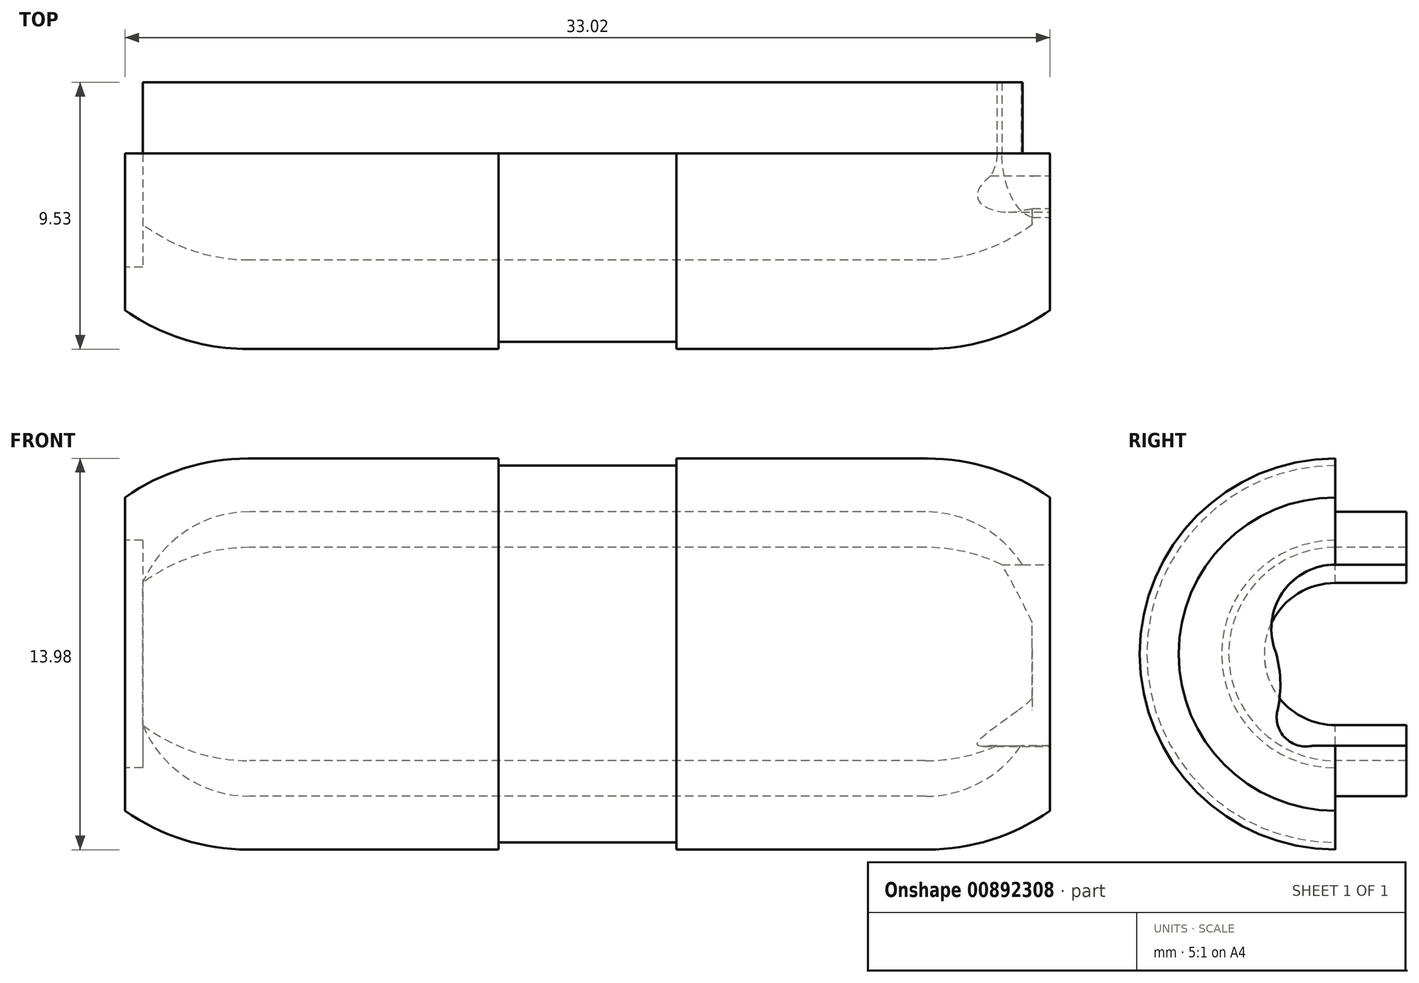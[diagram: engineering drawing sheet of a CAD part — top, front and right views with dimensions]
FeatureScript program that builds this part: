
annotation { "Feature Type Name" : "Feature", "Feature Type Description" : "" }
export const myFeature = defineFeature(function(context is Context, id is Id, definition is map)
    precondition{}
    {
        {
            var Q0;
            Q0=qCreatedBy(makeId("Front.planeOp"),FACE);
            var sketch = newSketch(context, id + "F0", { "sketchPlane" : qUnion([Q0])});
            skLineSegment(sketch, "E0.top", {"start": v(12.12, 6.98) * mm, "end": v(-12.12, 6.98) * mm});
            skPoint(sketch, "E0.middle", {"position": v(0, 0) * mm});
            skArc(sketch, "E1.filletArc", {"start": v(-12.12, 6.98) * mm, "mid": v(-16.24, 5.78) * mm, "end": v(-19.05, 2.54) * mm});
            skArc(sketch, "E2.filletArc", {"start": v(19.05, 2.54) * mm, "mid": v(16.24, 5.78) * mm, "end": v(12.12, 6.98) * mm});
            skLineSegment(sketch, "E3.top", {"start": v(12.06, 3.8) * mm, "end": v(-12.06, 3.8) * mm});
            skArc(sketch, "E4.filletArc", {"start": v(-12.06, 3.8) * mm, "mid": v(-14.07, 3.48) * mm, "end": v(-15.88, 2.54) * mm});
            skArc(sketch, "E5.filletArc", {"start": v(15.88, 2.54) * mm, "mid": v(14.07, 3.48) * mm, "end": v(12.06, 3.8) * mm});
            skLineSegment(sketch, "E6.top", {"start": v(-19.05, 2.54) * mm, "end": v(-15.88, 2.54) * mm});
            skPoint(sketch, "E7.orphan", {"position": v(-47.42, 2.54) * mm});
            skLineSegment(sketch, "E8.trimOffspring", {"start": v(15.88, 2.54) * mm, "end": v(19.05, 2.54) * mm});
            skSolve(sketch);
        }
        {
            var Q0;
            Q0=qCreatedBy(makeId("Top.planeOp"),FACE);
            var sketch = newSketch(context, id + "F1", { "sketchPlane" : qUnion([Q0])});
            skLineSegment(sketch, "E9", {"start": v(-41.86, 0) * mm, "end": v(38.58, 0) * mm, "construction": true});
            skSolve(sketch);
        }
        {
            var Q0;
            Q0 = qSketchRegion(id + "F0", true);
            var Q1;
            Q1=sQuery(id+"F1.wireOp",EDGE,"E9");
            revolve(context, id + "F2", {"surfaceOperationType" : NewSurfaceOperationType.NEW, "entities" : qUnion([Q0]), "axis" : qUnion([Q1]), "revolveType" : RevolveType.ONE_DIRECTION, "angle" : 180 * degree});
        }
        {
            var Q0;
            Q0=makeQuery(id+"F2.opRevolve","CAP_FACE",FACE,{"disambiguationData":[OSD([sQuery(id+"F0.wireOp",EDGE,"E0.top"),sQuery(id+"F0.wireOp",EDGE,"E1.filletArc"),sQuery(id+"F0.wireOp",EDGE,"E2.filletArc"),sQuery(id+"F0.wireOp",EDGE,"E3.top"),sQuery(id+"F0.wireOp",EDGE,"E4.filletArc"),sQuery(id+"F0.wireOp",EDGE,"E5.filletArc"),sQuery(id+"F0.wireOp",EDGE,"JIvlJlBu-vfLA-I6Gr-C8jU-59FBPmd7U8bv"),sQuery(id+"F0.wireOp",EDGE,"RInppC3X-QeJU-EZpC-KpJT-0cWvms3T49e7")])],"isStart":true});
            var sketch = newSketch(context, id + "F3", { "sketchPlane" : qUnion([Q0])});
            skLineSegment(sketch, "E10", {"start": v(-12.06, -3.8) * mm, "end": v(12.06, -3.8) * mm});
            skPoint(sketch, "E11.visualSharp", {"position": v(-15.87, -14.87) * mm});
            skArc(sketch, "E11.filletArc", {"start": v(-15.88, -2.54) * mm, "mid": v(-14.07, -3.48) * mm, "end": v(-12.06, -3.8) * mm});
            skArc(sketch, "E12", {"start": v(12.06, -3.8) * mm, "mid": v(14.07, -3.48) * mm, "end": v(15.87, -2.54) * mm});
            skLineSegment(sketch, "E13", {"start": v(-12.06, -5.08) * mm, "end": v(12.06, -5.08) * mm});
            skPoint(sketch, "E14.visualSharp", {"position": v(-15.87, -15.92) * mm});
            skArc(sketch, "E14.filletArc", {"start": v(-15.88, -2.54) * mm, "mid": v(-14.35, -4.39) * mm, "end": v(-12.06, -5.08) * mm});
            skPoint(sketch, "E15.visualSharp", {"position": v(22.86, -13.97) * mm});
            skArc(sketch, "E15.filletArc", {"start": v(12.06, -5.08) * mm, "mid": v(14.35, -4.39) * mm, "end": v(15.87, -2.54) * mm});
            skArc(sketch, "E16.MirrorCS", {"start": v(12.06, 5.08) * mm, "mid": v(14.35, 4.39) * mm, "end": v(15.87, 2.54) * mm});
            skArc(sketch, "E17.MirrorCS", {"start": v(12.06, 3.8) * mm, "mid": v(14.07, 3.48) * mm, "end": v(15.87, 2.54) * mm});
            skArc(sketch, "E18.MirrorCS", {"start": v(-15.88, 2.54) * mm, "mid": v(-14.35, 4.39) * mm, "end": v(-12.06, 5.08) * mm});
            skArc(sketch, "E19.MirrorCS", {"start": v(-15.88, 2.54) * mm, "mid": v(-14.07, 3.48) * mm, "end": v(-12.06, 3.8) * mm});
            skLineSegment(sketch, "E20.MirrorCS", {"start": v(-12.06, 5.08) * mm, "end": v(12.06, 5.08) * mm});
            skLineSegment(sketch, "E21.MirrorCS", {"start": v(-12.06, 3.8) * mm, "end": v(12.06, 3.8) * mm});
            skSolve(sketch);
        }
        {
            var Q0;
            Q0 = qSketchRegion(id + "F3", true);
            extrude(context, id + "F4", {"entities" : qUnion([Q0]), "operationType" : NewBodyOperationType.ADD, "depth" : 2.54 * mm, "offsetDistance" : 25.4 * mm});
        }
        {
            var Q0;
            Q0=qCreatedBy(makeId("Front.planeOp"),FACE);
            var sketch = newSketch(context, id + "F5", { "sketchPlane" : qUnion([Q0])});
            skLineSegment(sketch, "E22", {"start": v(42.24, 0) * mm, "end": v(-46.74, 0) * mm, "construction": true});
            skSolve(sketch);
        }
        {
            var Q0;
            Q0=makeQuery(id+"F2.opRevolve","CAP_FACE",FACE,{"disambiguationData":[OSD([sQuery(id+"F0.wireOp",EDGE,"E0.top"),sQuery(id+"F0.wireOp",EDGE,"E1.filletArc"),sQuery(id+"F0.wireOp",EDGE,"E2.filletArc"),sQuery(id+"F0.wireOp",EDGE,"E3.top"),sQuery(id+"F0.wireOp",EDGE,"E4.filletArc"),sQuery(id+"F0.wireOp",EDGE,"E5.filletArc"),sQuery(id+"F0.wireOp",EDGE,"E6.top"),sQuery(id+"F0.wireOp",EDGE,"E8.trimOffspring")])],"isStart":true});
            var sketch = newSketch(context, id + "F6", { "sketchPlane" : qUnion([Q0])});
            skLineSegment(sketch, "E23.bottom", {"start": v(3.18, 6.73) * mm, "end": v(-3.17, 6.73) * mm});
            skLineSegment(sketch, "E23.top", {"start": v(3.18, 7.24) * mm, "end": v(-3.17, 7.24) * mm});
            skLineSegment(sketch, "E23.left", {"start": v(3.18, 6.73) * mm, "end": v(3.18, 7.24) * mm});
            skLineSegment(sketch, "E23.right", {"start": v(-3.17, 6.73) * mm, "end": v(-3.17, 7.24) * mm});
            skPoint(sketch, "E23.middle", {"position": v(0, 6.98) * mm});
            skSolve(sketch);
        }
        {
            var Q0;
            Q0 = qSketchRegion(id + "F6", true);
            var Q1;
            Q1=sQuery(id+"F5.wireOp",EDGE,"E22");
            revolve(context, id + "F7", {"operationType" : NewBodyOperationType.REMOVE, "surfaceOperationType" : NewSurfaceOperationType.NEW, "entities" : qUnion([Q0]), "axis" : qUnion([Q1]), "revolveType" : RevolveType.FULL, "oppositeDirection" : true});
        }
        {
            var Q0;
            Q0=makeQuery(id+"F2.opRevolve","CAP_FACE",FACE,{"disambiguationData":[OSD([sQuery(id+"F0.wireOp",EDGE,"E0.top"),sQuery(id+"F0.wireOp",EDGE,"E1.filletArc"),sQuery(id+"F0.wireOp",EDGE,"E2.filletArc"),sQuery(id+"F0.wireOp",EDGE,"E3.top"),sQuery(id+"F0.wireOp",EDGE,"E4.filletArc"),sQuery(id+"F0.wireOp",EDGE,"E5.filletArc"),sQuery(id+"F0.wireOp",EDGE,"E6.top"),sQuery(id+"F0.wireOp",EDGE,"E8.trimOffspring")])],"isStart":true});
            var sketch = newSketch(context, id + "F8", { "sketchPlane" : qUnion([Q0])});
            skLineSegment(sketch, "E24.bottom", {"start": v(-19.05, 5.6) * mm, "end": v(-16.51, 5.6) * mm});
            skLineSegment(sketch, "E24.top", {"start": v(-19.05, -5.6) * mm, "end": v(-16.51, -5.6) * mm});
            skLineSegment(sketch, "E24.left", {"start": v(-19.05, 5.6) * mm, "end": v(-19.05, -5.6) * mm});
            skLineSegment(sketch, "E24.right", {"start": v(-16.51, 5.6) * mm, "end": v(-16.51, -5.6) * mm});
            skLineSegment(sketch, "E25.MirrorCS", {"start": v(19.05, -5.6) * mm, "end": v(16.51, -5.6) * mm});
            skLineSegment(sketch, "E26.MirrorCS", {"start": v(16.51, 5.6) * mm, "end": v(16.51, -5.6) * mm});
            skLineSegment(sketch, "E27.MirrorCS", {"start": v(19.05, 5.6) * mm, "end": v(16.51, 5.6) * mm});
            skLineSegment(sketch, "E28.MirrorCS", {"start": v(19.05, 5.6) * mm, "end": v(19.05, -5.6) * mm});
            skSolve(sketch);
        }
        {
            var Q0;
            Q0 = qSketchRegion(id + "F8", true);
            extrude(context, id + "F9", {"entities" : qUnion([Q0]), "operationType" : NewBodyOperationType.REMOVE, "oppositeDirection" : true, "depth" : 25.4 * mm, "offsetDistance" : 25.4 * mm});
        }
        {
            var Q0;
            Q0=makeQuery(id+"F9.boolean.opBoolean","COPY",FACE,{"derivedFrom":makeQuery(id+"F9.opExtrude","SWEPT_FACE",FACE,{"disambiguationData":[OSD([sQuery(id+"F8.wireOp",EDGE,"E24.right")])]})});
            var sketch = newSketch(context, id + "F10", { "sketchPlane" : qUnion([Q0])});
            skArc(sketch, "E29", {"start": v(0, 2.54) * mm, "mid": v(-2.54, 0) * mm, "end": v(0, -2.54) * mm});
            skLineSegment(sketch, "E30", {"start": v(0, 2.54) * mm, "end": v(0, -2.54) * mm});
            skSolve(sketch);
        }
        {
            var Q0;
            Q0 = qSketchRegion(id + "F10", true);
            var Q1;
            Q1=makeQuery(id+"F2.opRevolve","SWEPT_FACE",FACE,{"disambiguationData":[OSD([sQuery(id+"F0.wireOp",EDGE,"E8.trimOffspring")])]});
            var Q2;
            {var subQ0=sQuery(id+"F0.wireOp",EDGE,"E8.trimOffspring");Q2=makeQuery(id+"F4.boolean.opBoolean","MERGE",VERTEX,{"derivedFrom":[makeQuery(id+"F2.opRevolve","CAP_VERTEX",VERTEX,{"disambiguationData":[OSD([sQuery(id+"F0.wireOp",EDGE,"E5.filletArc"),subQ0])],"isStart":true}),makeQuery(id+"F4.opExtrude","CAP_VERTEX",VERTEX,{"disambiguationData":[OSD([subQ0,sQuery(id+"F3.wireOp",EDGE,"E18.MirrorCS"),sQuery(id+"F3.wireOp",EDGE,"E19.MirrorCS")])],"isStart":true})]});}
            extrude(context, id + "F11", {"entities" : qUnion([Q0]), "operationType" : NewBodyOperationType.ADD, "endBound" : BoundingType.UP_TO_VERTEX, "oppositeDirection" : true, "depth" : 25.4 * mm, "endBoundEntityFace" : qUnion([Q1]), "endBoundEntityVertex" : qUnion([Q2]), "offsetDistance" : 25.4 * mm});
        }
        {
            var Q0;
            Q0=makeQuery(id+"F11.boolean.opBoolean","MERGE",FACE,{"derivedFrom":[makeQuery(id+"F9.boolean.opBoolean","COPY",FACE,{"derivedFrom":makeQuery(id+"F9.opExtrude","SWEPT_FACE",FACE,{"disambiguationData":[OSD([sQuery(id+"F8.wireOp",EDGE,"E24.right")])]})}),makeQuery(id+"F11.opExtrude","CAP_FACE",FACE,{"disambiguationData":[OSD([sQuery(id+"F10.wireOp",EDGE,"E29"),sQuery(id+"F10.wireOp",EDGE,"E30")])],"isStart":true})]});
            var sketch = newSketch(context, id + "F12", { "sketchPlane" : qUnion([Q0])});
            skArc(sketch, "E31", {"start": v(2.17, 0.2) * mm, "mid": v(0, 3.2) * mm, "end": v(-2.17, 0.2) * mm});
            skArc(sketch, "E32", {"start": v(0.84, -3.28) * mm, "mid": v(1.8, -2.99) * mm, "end": v(2.07, -2.02) * mm});
            skArc(sketch, "E33", {"start": v(-2.07, -2.02) * mm, "mid": v(-1.8, -2.99) * mm, "end": v(-0.84, -3.28) * mm});
            skPoint(sketch, "E34.visualSharp", {"position": v(-0.72, -1.26) * mm});
            skArc(sketch, "E34.filletArc", {"start": v(-2.07, -2.02) * mm, "mid": v(-1.97, -0.9) * mm, "end": v(-2.17, 0.2) * mm});
            skPoint(sketch, "E35.visualSharp", {"position": v(0.72, -1.26) * mm});
            skArc(sketch, "E35.filletArc", {"start": v(2.17, 0.2) * mm, "mid": v(1.97, -0.9) * mm, "end": v(2.07, -2.02) * mm});
            skPoint(sketch, "E36.visualSharp", {"position": v(0, -2.26) * mm});
            skArc(sketch, "E36.filletArc", {"start": v(0.84, -3.28) * mm, "mid": v(0, -3.2) * mm, "end": v(-0.84, -3.28) * mm});
            skLineSegment(sketch, "E37", {"start": v(0, -3.2) * mm, "end": v(0, 3.2) * mm, "construction": true});
            skPoint(sketch, "E38", {"position": v(0, 0) * mm});
            skSolve(sketch);
        }
        {
            var Q0;
            Q0 = qSketchRegion(id + "F12", true);
            var Q1;
            Q1=makeQuery(id+"F11.opExtrude","CAP_FACE",FACE,{"disambiguationData":[OSD([sQuery(id+"F10.wireOp",EDGE,"E29"),sQuery(id+"F10.wireOp",EDGE,"E30")])],"isStart":false});
            extrude(context, id + "F13", {"entities" : qUnion([Q0]), "operationType" : NewBodyOperationType.REMOVE, "endBound" : BoundingType.UP_TO_SURFACE, "oppositeDirection" : true, "depth" : 25.4 * mm, "endBoundEntityFace" : qUnion([Q1]), "offsetDistance" : 25.4 * mm});
        }
        {
            var Q0;
            Q0=makeQuery(id+"F9.boolean.opBoolean","COPY",FACE,{"derivedFrom":makeQuery(id+"F9.opExtrude","SWEPT_FACE",FACE,{"disambiguationData":[OSD([sQuery(id+"F8.wireOp",EDGE,"E26.MirrorCS")])]})});
            var sketch = newSketch(context, id + "F14", { "sketchPlane" : qUnion([Q0])});
            skArc(sketch, "E39", {"start": v(0, -2.54) * mm, "mid": v(2.54, 0) * mm, "end": v(0, 2.54) * mm});
            skLineSegment(sketch, "E40", {"start": v(0, -2.54) * mm, "end": v(0, 2.54) * mm});
            skSolve(sketch);
        }
        {
            var Q0;
            Q0 = qSketchRegion(id + "F14", true);
            var Q1;
            Q1=makeQuery(id+"F4.boolean.opBoolean","MERGE",VERTEX,{"derivedFrom":[makeQuery(id+"F2.opRevolve","CAP_VERTEX",VERTEX,{"disambiguationData":[OSD([sQuery(id+"F0.wireOp",EDGE,"E4.filletArc"),sQuery(id+"F0.wireOp",EDGE,"E6.top")])],"isStart":false}),makeQuery(id+"F4.opExtrude","CAP_VERTEX",VERTEX,{"disambiguationData":[OSD([sQuery(id+"F3.wireOp",EDGE,"E12"),sQuery(id+"F3.wireOp",EDGE,"E15.filletArc")])],"isStart":true})]});
            extrude(context, id + "F15", {"entities" : qUnion([Q0]), "operationType" : NewBodyOperationType.ADD, "endBound" : BoundingType.UP_TO_VERTEX, "oppositeDirection" : true, "depth" : 25.4 * mm, "endBoundEntityVertex" : qUnion([Q1]), "offsetDistance" : 25.4 * mm});
        }
        {
            var Q0;
            Q0=makeQuery(id+"F15.boolean.opBoolean","MERGE",FACE,{"derivedFrom":[makeQuery(id+"F9.boolean.opBoolean","COPY",FACE,{"derivedFrom":makeQuery(id+"F9.opExtrude","SWEPT_FACE",FACE,{"disambiguationData":[OSD([sQuery(id+"F8.wireOp",EDGE,"E26.MirrorCS")])]})}),makeQuery(id+"F15.opExtrude","CAP_FACE",FACE,{"disambiguationData":[OSD([sQuery(id+"F14.wireOp",EDGE,"E39"),sQuery(id+"F14.wireOp",EDGE,"E40")])],"isStart":true})]});
            var sketch = newSketch(context, id + "F16", { "sketchPlane" : qUnion([Q0])});
            skCircle(sketch, "E41", {"center": v(0, 0) * mm, "radius": 4.06 * mm});
            skSolve(sketch);
        }
        {
            var Q0;
            Q0 = qSketchRegion(id + "F16", true);
            var Q1;
            Q1=makeQuery(id+"F15.opExtrude","CAP_FACE",FACE,{"disambiguationData":[OSD([sQuery(id+"F14.wireOp",EDGE,"E39"),sQuery(id+"F14.wireOp",EDGE,"E40")])],"isStart":false});
            extrude(context, id + "F17", {"entities" : qUnion([Q0]), "operationType" : NewBodyOperationType.REMOVE, "endBound" : BoundingType.UP_TO_SURFACE, "oppositeDirection" : true, "depth" : 25.4 * mm, "endBoundEntityFace" : qUnion([Q1]), "offsetDistance" : 25.4 * mm});
        }
        {
            var Q0;
            Q0=makeQuery(id+"F11.boolean.opBoolean","MERGE",FACE,{"derivedFrom":[makeQuery(id+"F9.boolean.opBoolean","COPY",FACE,{"derivedFrom":makeQuery(id+"F9.opExtrude","SWEPT_FACE",FACE,{"disambiguationData":[OSD([sQuery(id+"F8.wireOp",EDGE,"E24.right")])]})}),makeQuery(id+"F11.opExtrude","CAP_FACE",FACE,{"disambiguationData":[OSD([sQuery(id+"F10.wireOp",EDGE,"E29"),sQuery(id+"F10.wireOp",EDGE,"E30")])],"isStart":true})]});
            var sketch = newSketch(context, id + "F18", { "sketchPlane" : qUnion([Q0])});
            skArc(sketch, "E42", {"start": v(0, 3.2) * mm, "mid": v(-1.86, 2.24) * mm, "end": v(-2.16, 0.16) * mm});
            skPoint(sketch, "E42.first.point", {"position": v(-0.31, 3.17) * mm});
            skPoint(sketch, "E42.second.point", {"position": v(-1.42, 2.7) * mm});
            skPoint(sketch, "E42.third.point", {"position": v(-2.24, 1.34) * mm});
            skArc(sketch, "E43", {"start": v(-2.06, -2) * mm, "mid": v(-1.79, -3) * mm, "end": v(-0.8, -3.27) * mm});
            skPoint(sketch, "E43.first.point", {"position": v(-2.06, -2.53) * mm});
            skPoint(sketch, "E43.second.point", {"position": v(-1.45, -3.22) * mm});
            skPoint(sketch, "E43.third.point", {"position": v(-1.26, -3.28) * mm});
            skArc(sketch, "E44", {"start": v(0, -2.23) * mm, "mid": v(0, -2.24) * mm, "end": v(0, -2.26) * mm});
            skPoint(sketch, "E44.first.point", {"position": v(0, -2.26) * mm});
            skPoint(sketch, "E44.second.point", {"position": v(0.87, -1.2) * mm});
            skPoint(sketch, "E44.third.point", {"position": v(1.43, -3.2) * mm});
            skPoint(sketch, "E45.visualSharp", {"position": v(-0.72, -1.26) * mm});
            skArc(sketch, "E45.filletArc", {"start": v(-2.06, -2) * mm, "mid": v(-1.96, -0.91) * mm, "end": v(-2.16, 0.16) * mm});
            skPoint(sketch, "E46.visualSharp", {"position": v(0.56, -1.3) * mm});
            skLineSegment(sketch, "E47", {"start": v(-1.3, -3.27) * mm, "end": v(2.54, -3.27) * mm});
            skLineSegment(sketch, "E48", {"start": v(2.54, -3.27) * mm, "end": v(2.54, 3.2) * mm});
            skLineSegment(sketch, "E49", {"start": v(2.54, 3.2) * mm, "end": v(0, 3.2) * mm});
            skArc(sketch, "E50.trimOffspring", {"start": v(1.04, -3.27) * mm, "mid": v(1.24, -3.25) * mm, "end": v(1.43, -3.2) * mm});
            skArc(sketch, "E51.trimOffspring", {"start": v(0, -2.26) * mm, "mid": v(0, -2.24) * mm, "end": v(0, -2.23) * mm});
            skSolve(sketch);
        }
        {
            var Q0;
            Q0 = qSketchRegion(id + "F18", true);
            var Q1;
            Q1=makeQuery(id+"F4.boolean.opBoolean","MERGE",VERTEX,{"derivedFrom":[makeQuery(id+"F2.opRevolve","CAP_VERTEX",VERTEX,{"disambiguationData":[OSD([sQuery(id+"F0.wireOp",EDGE,"E3.top"),sQuery(id+"F0.wireOp",EDGE,"E5.filletArc")])],"isStart":true}),makeQuery(id+"F4.opExtrude","CAP_VERTEX",VERTEX,{"disambiguationData":[OSD([sQuery(id+"F3.wireOp",EDGE,"E19.MirrorCS"),sQuery(id+"F3.wireOp",EDGE,"E21.MirrorCS")])],"isStart":true})]});
            extrude(context, id + "F19", {"entities" : qUnion([Q0]), "operationType" : NewBodyOperationType.REMOVE, "endBound" : BoundingType.UP_TO_VERTEX, "oppositeDirection" : true, "depth" : 25.4 * mm, "endBoundEntityVertex" : qUnion([Q1]), "offsetDistance" : 25.4 * mm});
        }
    });
